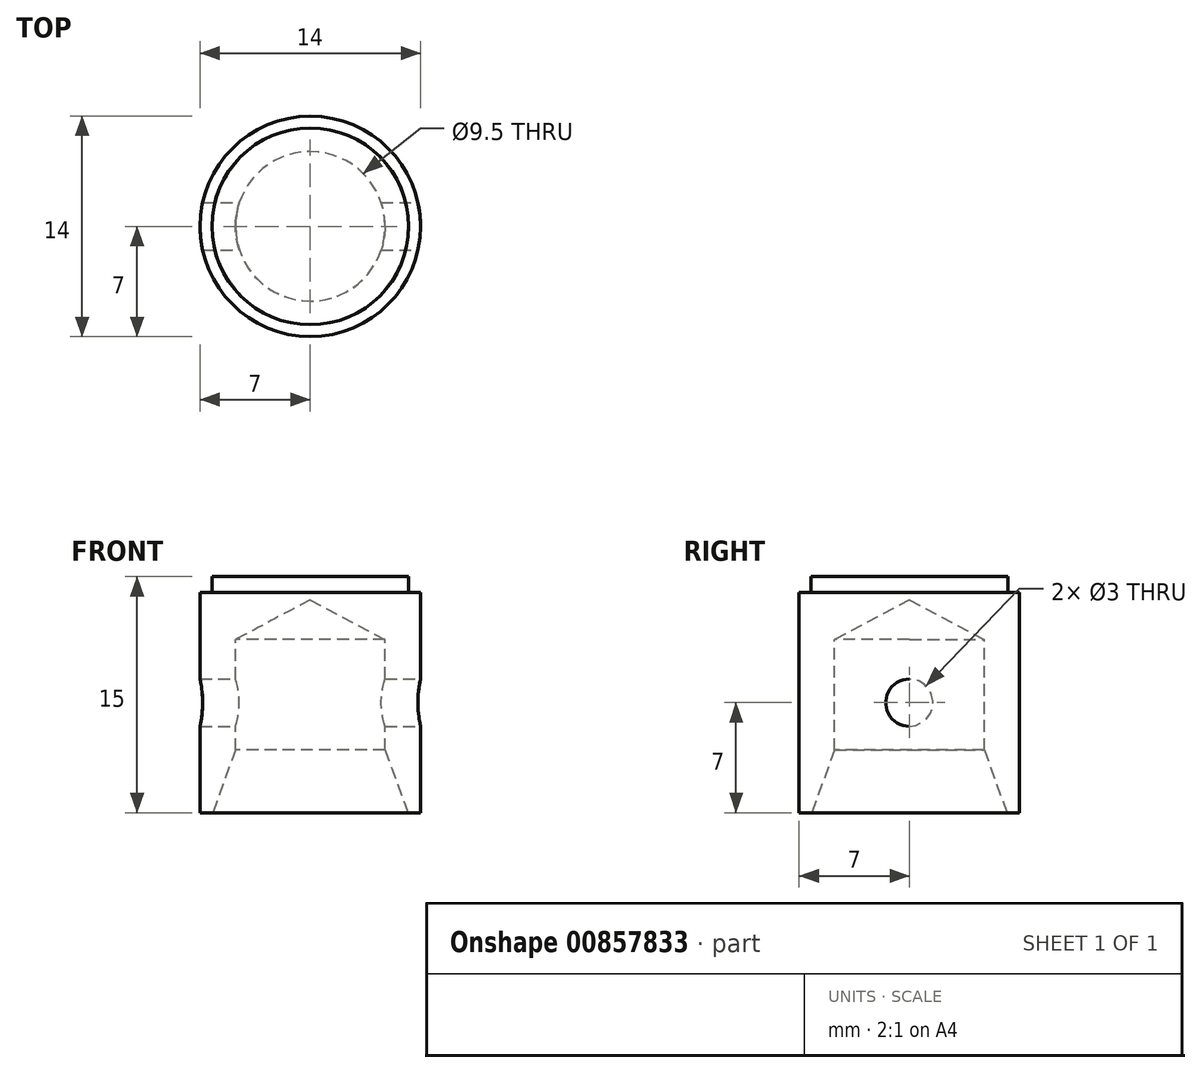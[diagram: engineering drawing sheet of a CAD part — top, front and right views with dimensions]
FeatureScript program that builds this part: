
annotation { "Feature Type Name" : "Feature", "Feature Type Description" : "" }
export const myFeature = defineFeature(function(context is Context, id is Id, definition is map)
    precondition{}
    {
        {
            var Q0;
            Q0=qCreatedBy(makeId("Front.planeOp"),FACE);
            var sketch = newSketch(context, id + "F0", { "sketchPlane" : qUnion([Q0])});
            skLineSegment(sketch, "E0", {"start": v(-7, 0) * mm, "end": v(-7, 14) * mm});
            skLineSegment(sketch, "E1", {"start": v(-7, 14) * mm, "end": v(-6.25, 14) * mm});
            skLineSegment(sketch, "E2", {"start": v(-6.25, 14) * mm, "end": v(-6.25, 15) * mm});
            skLineSegment(sketch, "E3", {"start": v(-6.25, 15) * mm, "end": v(0, 15) * mm});
            skLineSegment(sketch, "E4", {"start": v(-4.75, 11) * mm, "end": v(0, 13.53) * mm});
            skLineSegment(sketch, "E5", {"start": v(-7, 0) * mm, "end": v(-6.2, 0) * mm});
            skLineSegment(sketch, "E6", {"start": v(-6.2, 0) * mm, "end": v(-4.75, 3.98) * mm});
            skLineSegment(sketch, "E7", {"start": v(-4.75, 3.98) * mm, "end": v(-4.75, 11) * mm});
            skLineSegment(sketch, "E8", {"start": v(-4.75, 3.98) * mm, "end": v(-4.75, -2.44) * mm, "construction": true});
            skLineSegment(sketch, "E9", {"start": v(0, 15) * mm, "end": v(0, 13.53) * mm});
            skPoint(sketch, "E10.orphan", {"position": v(0.9, 14) * mm});
            skSolve(sketch);
        }
        {
            var Q0;
            Q0=makeQuery(id+"F0.imprint","IMPRINT",FACE,{"disambiguationData":[TD([[makeQuery(id+"F0.imprint","IMPRINT",EDGE,{"derivedFrom":sQuery(id+"F0.wireOp",EDGE,"E0")}),-1.0]])]});
            var Q1;
            Q1=sQuery(id+"F0.wireOp",EDGE,"E9");
            revolve(context, id + "F1", {"surfaceOperationType" : NewSurfaceOperationType.NEW, "entities" : qUnion([Q0]), "axis" : qUnion([Q1]), "revolveType" : RevolveType.FULL});
        }
        {
            var Q0;
            Q0=qCreatedBy(makeId("Right.planeOp"),FACE);
            var sketch = newSketch(context, id + "F2", { "sketchPlane" : qUnion([Q0])});
            skCircle(sketch, "E11", {"center": v(0, 7) * mm, "radius": 1.5 * mm});
            skSolve(sketch);
        }
        {
            var Q0;
            Q0=makeQuery(id+"F2.imprint","IMPRINT",FACE,{"disambiguationData":[TD([[makeQuery(id+"F2.imprint","IMPRINT",EDGE,{"derivedFrom":sQuery(id+"F2.wireOp",EDGE,"E11")}),1.0]])]});
            extrude(context, id + "F3", {"entities" : qUnion([Q0]), "operationType" : NewBodyOperationType.REMOVE, "endBound" : BoundingType.THROUGH_ALL, "oppositeDirection" : true, "depth" : 25 * mm, "offsetDistance" : 25 * mm, "hasSecondDirection" : true, "secondDirectionBound" : SecondDirectionBoundingType.THROUGH_ALL, "secondDirectionOppositeDirection" : false, "secondDirectionDepth" : 25 * mm});
        }
    });
